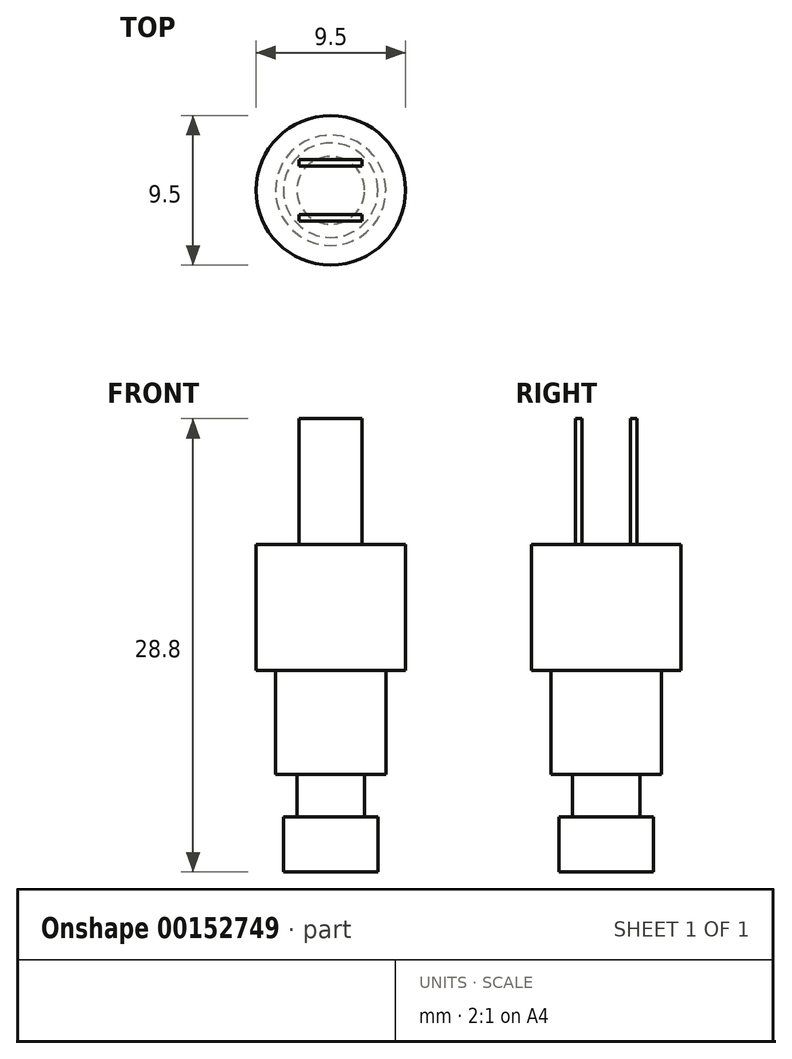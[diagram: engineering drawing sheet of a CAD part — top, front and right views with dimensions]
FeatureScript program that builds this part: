
annotation { "Feature Type Name" : "Feature", "Feature Type Description" : "" }
export const myFeature = defineFeature(function(context is Context, id is Id, definition is map)
    precondition{}
    {
        {
            var Q0;
            Q0=qCreatedBy(makeId("Top.planeOp"),FACE);
            var sketch = newSketch(context, id + "F0", { "sketchPlane" : qUnion([Q0])});
            skCircle(sketch, "E0", {"center": v(0, 0) * mm, "radius": 3 * mm});
            skSolve(sketch);
        }
        {
            var Q0;
            Q0 = qSketchRegion(id + "F0", true);
            extrude(context, id + "F1", {"entities" : qUnion([Q0]), "depth" : 3.5 * mm});
        }
        {
            var Q0;
            Q0=makeQuery(id+"F1.opExtrude","CAP_FACE",FACE,{"disambiguationData":[OSD([sQuery(id+"F0.wireOp",EDGE,"E0")])],"isStart":false});
            var sketch = newSketch(context, id + "F2", { "sketchPlane" : qUnion([Q0])});
            skCircle(sketch, "E1", {"center": v(0, 0) * mm, "radius": 2.15 * mm});
            skSolve(sketch);
        }
        {
            var Q0;
            Q0 = qSketchRegion(id + "F2", true);
            extrude(context, id + "F3", {"entities" : qUnion([Q0]), "operationType" : NewBodyOperationType.ADD, "depth" : 2.7 * mm});
        }
        {
            var Q0;
            Q0=makeQuery(id+"F3.opExtrude","CAP_FACE",FACE,{"disambiguationData":[OSD([sQuery(id+"F2.wireOp",EDGE,"E1")])],"isStart":false});
            var sketch = newSketch(context, id + "F4", { "sketchPlane" : qUnion([Q0])});
            skCircle(sketch, "E2", {"center": v(0, 0) * mm, "radius": 3.5 * mm});
            skSolve(sketch);
        }
        {
            var Q0;
            Q0 = qSketchRegion(id + "F4", true);
            extrude(context, id + "F5", {"entities" : qUnion([Q0]), "operationType" : NewBodyOperationType.ADD, "depth" : 6.6 * mm});
        }
        {
            var Q0;
            Q0=makeQuery(id+"F5.opExtrude","CAP_FACE",FACE,{"disambiguationData":[OSD([sQuery(id+"F4.wireOp",EDGE,"E2")])],"isStart":false});
            var sketch = newSketch(context, id + "F6", { "sketchPlane" : qUnion([Q0])});
            skCircle(sketch, "E3", {"center": v(0, 0) * mm, "radius": 4.75 * mm});
            skSolve(sketch);
        }
        {
            var Q0;
            Q0 = qSketchRegion(id + "F6", true);
            extrude(context, id + "F7", {"entities" : qUnion([Q0]), "operationType" : NewBodyOperationType.ADD, "depth" : 8 * mm});
        }
        {
            var Q0;
            Q0=makeQuery(id+"F7.opExtrude","CAP_FACE",FACE,{"disambiguationData":[OSD([sQuery(id+"F6.wireOp",EDGE,"E3")])],"isStart":false});
            var sketch = newSketch(context, id + "F8", { "sketchPlane" : qUnion([Q0])});
            skLineSegment(sketch, "E4", {"start": v(0, 0) * mm, "end": v(0, -1.75) * mm, "construction": true});
            skLineSegment(sketch, "E5", {"start": v(0, 0) * mm, "end": v(0, 1.75) * mm, "construction": true});
            skLineSegment(sketch, "E6.bottom", {"start": v(-2, -1.55) * mm, "end": v(2, -1.55) * mm});
            skLineSegment(sketch, "E6.top", {"start": v(-2, -1.95) * mm, "end": v(2, -1.95) * mm});
            skLineSegment(sketch, "E6.left", {"start": v(-2, -1.55) * mm, "end": v(-2, -1.95) * mm});
            skLineSegment(sketch, "E6.right", {"start": v(2, -1.55) * mm, "end": v(2, -1.95) * mm});
            skPoint(sketch, "E6.middle", {"position": v(0, -1.75) * mm});
            skLineSegment(sketch, "E7.bottom", {"start": v(-2, 1.95) * mm, "end": v(2, 1.95) * mm});
            skLineSegment(sketch, "E7.top", {"start": v(-2, 1.55) * mm, "end": v(2, 1.55) * mm});
            skLineSegment(sketch, "E7.left", {"start": v(-2, 1.95) * mm, "end": v(-2, 1.55) * mm});
            skLineSegment(sketch, "E7.right", {"start": v(2, 1.95) * mm, "end": v(2, 1.55) * mm});
            skPoint(sketch, "E7.middle", {"position": v(0, 1.75) * mm});
            skSolve(sketch);
        }
        {
            var Q0;
            Q0 = qSketchRegion(id + "F8", true);
            extrude(context, id + "F9", {"entities" : qUnion([Q0]), "operationType" : NewBodyOperationType.ADD, "depth" : 8 * mm});
        }
    });
